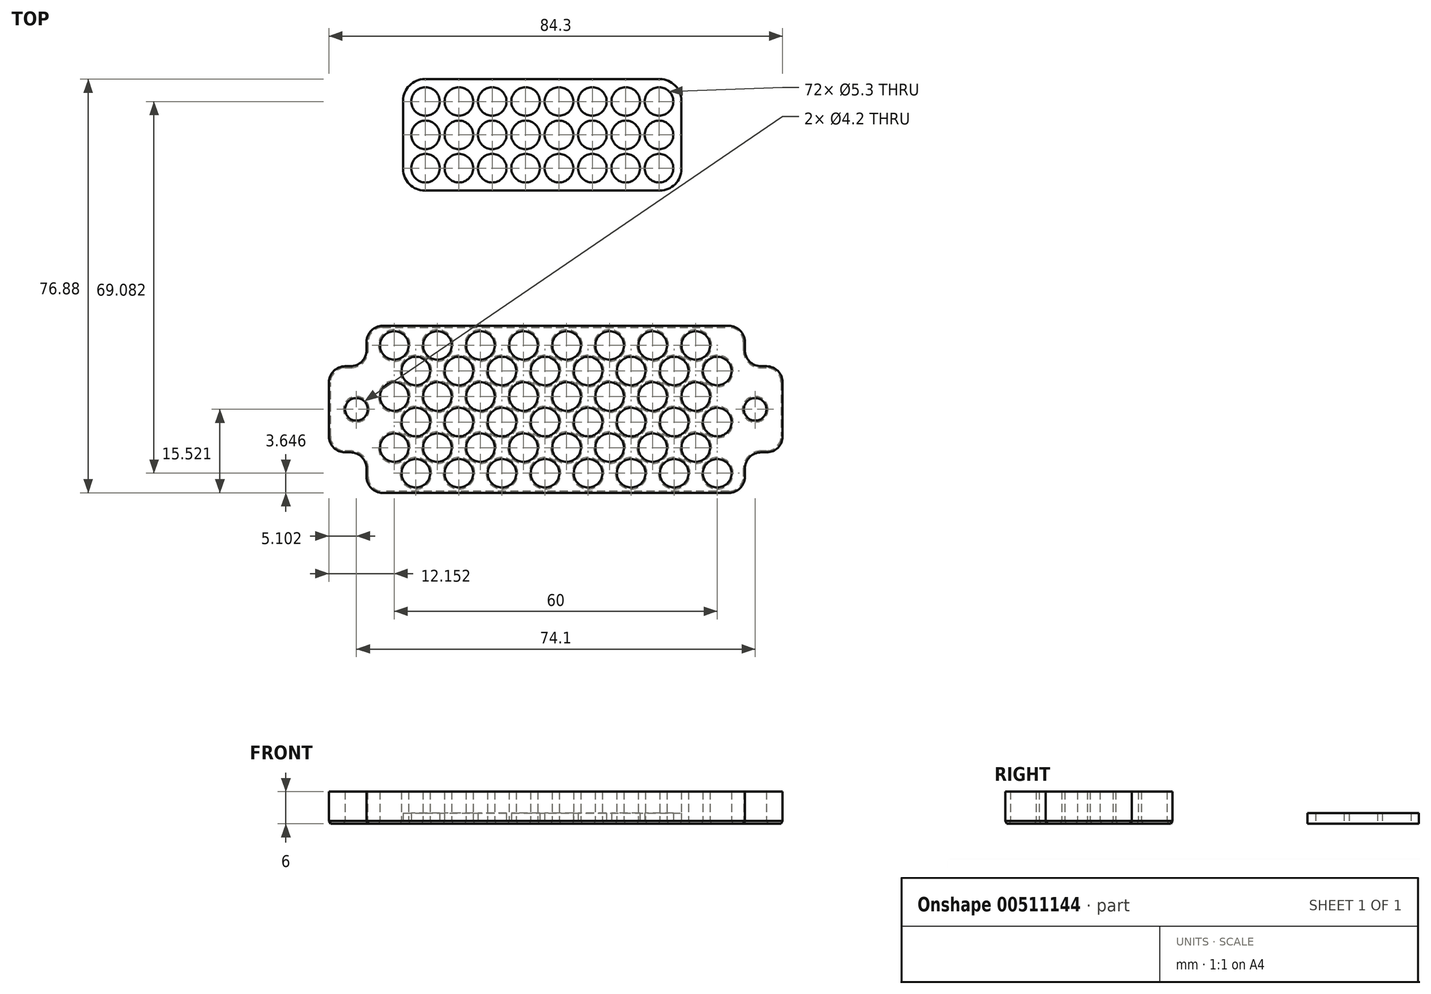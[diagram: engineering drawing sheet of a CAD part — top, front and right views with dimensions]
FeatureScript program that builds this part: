
annotation { "Feature Type Name" : "Feature", "Feature Type Description" : "" }
export const myFeature = defineFeature(function(context is Context, id is Id, definition is map)
    precondition{}
    {
        {
            var Q0;
            Q0=qCreatedBy(makeId("Top.planeOp"),FACE);
            var sketch = newSketch(context, id + "F0", { "sketchPlane" : qUnion([Q0])});
            skCircle(sketch, "E0", {"center": v(-32.47, 32.1) * mm, "radius": 2.65 * mm});
            skCircle(sketch, "E1.0.1.0", {"center": v(-32.47, 25.9) * mm, "radius": 2.65 * mm});
            skCircle(sketch, "E1.0.2.0", {"center": v(-32.47, 19.7) * mm, "radius": 2.65 * mm});
            skCircle(sketch, "E1.1.0.0", {"center": v(-26.27, 32.1) * mm, "radius": 2.65 * mm});
            skCircle(sketch, "E1.1.1.0", {"center": v(-26.27, 25.9) * mm, "radius": 2.65 * mm});
            skCircle(sketch, "E1.1.2.0", {"center": v(-26.27, 19.7) * mm, "radius": 2.65 * mm});
            skCircle(sketch, "E1.2.0.0", {"center": v(-20.07, 32.1) * mm, "radius": 2.65 * mm});
            skCircle(sketch, "E1.2.1.0", {"center": v(-20.07, 25.9) * mm, "radius": 2.65 * mm});
            skCircle(sketch, "E1.2.2.0", {"center": v(-20.07, 19.7) * mm, "radius": 2.65 * mm});
            skCircle(sketch, "E1.3.0.0", {"center": v(-13.87, 32.1) * mm, "radius": 2.65 * mm});
            skCircle(sketch, "E1.3.1.0", {"center": v(-13.87, 25.9) * mm, "radius": 2.65 * mm});
            skCircle(sketch, "E1.3.2.0", {"center": v(-13.87, 19.7) * mm, "radius": 2.65 * mm});
            skCircle(sketch, "E1.4.0.0", {"center": v(-7.67, 32.1) * mm, "radius": 2.65 * mm});
            skCircle(sketch, "E1.4.1.0", {"center": v(-7.67, 25.9) * mm, "radius": 2.65 * mm});
            skCircle(sketch, "E1.4.2.0", {"center": v(-7.67, 19.7) * mm, "radius": 2.65 * mm});
            skCircle(sketch, "E1.5.0.0", {"center": v(-1.47, 32.1) * mm, "radius": 2.65 * mm});
            skCircle(sketch, "E1.5.1.0", {"center": v(-1.47, 25.9) * mm, "radius": 2.65 * mm});
            skCircle(sketch, "E1.5.2.0", {"center": v(-1.47, 19.7) * mm, "radius": 2.65 * mm});
            skCircle(sketch, "E1.6.0.0", {"center": v(4.73, 32.1) * mm, "radius": 2.65 * mm});
            skCircle(sketch, "E1.6.1.0", {"center": v(4.73, 25.9) * mm, "radius": 2.65 * mm});
            skCircle(sketch, "E1.6.2.0", {"center": v(4.73, 19.7) * mm, "radius": 2.65 * mm});
            skCircle(sketch, "E1.7.0.0", {"center": v(10.93, 32.1) * mm, "radius": 2.65 * mm});
            skCircle(sketch, "E1.7.1.0", {"center": v(10.93, 25.9) * mm, "radius": 2.65 * mm});
            skCircle(sketch, "E1.7.2.0", {"center": v(10.93, 19.7) * mm, "radius": 2.65 * mm});
            skLineSegment(sketch, "E1.direction1", {"start": v(-32.47, 32.1) * mm, "end": v(-26.27, 32.1) * mm, "construction": true});
            skLineSegment(sketch, "E1.direction2", {"start": v(-32.47, 32.1) * mm, "end": v(-32.47, 25.9) * mm, "construction": true});
            skLineSegment(sketch, "E2.bottom", {"start": v(-32.62, 36.25) * mm, "end": v(11.08, 36.25) * mm});
            skLineSegment(sketch, "E2.top", {"start": v(-32.62, 15.55) * mm, "end": v(11.08, 15.55) * mm});
            skLineSegment(sketch, "E2.left", {"start": v(-36.62, 32.25) * mm, "end": v(-36.62, 19.55) * mm});
            skLineSegment(sketch, "E2.right", {"start": v(15.08, 32.25) * mm, "end": v(15.08, 19.55) * mm});
            skPoint(sketch, "E3.visualSharp", {"position": v(-36.62, 36.25) * mm});
            skArc(sketch, "E3.filletArc", {"start": v(-32.62, 36.25) * mm, "mid": v(-35.45, 35.08) * mm, "end": v(-36.62, 32.25) * mm});
            skPoint(sketch, "E4.visualSharp", {"position": v(-36.62, 15.55) * mm});
            skArc(sketch, "E4.filletArc", {"start": v(-36.62, 19.55) * mm, "mid": v(-35.45, 16.72) * mm, "end": v(-32.62, 15.55) * mm});
            skPoint(sketch, "E5.visualSharp", {"position": v(15.08, 15.55) * mm});
            skArc(sketch, "E5.filletArc", {"start": v(11.08, 15.55) * mm, "mid": v(13.9, 16.72) * mm, "end": v(15.08, 19.55) * mm});
            skPoint(sketch, "E6.visualSharp", {"position": v(15.08, 36.25) * mm});
            skArc(sketch, "E6.filletArc", {"start": v(15.08, 32.25) * mm, "mid": v(13.9, 35.08) * mm, "end": v(11.08, 36.25) * mm});
            skCircle(sketch, "E7", {"center": v(-38.27, -13.23) * mm, "radius": 2.65 * mm});
            skCircle(sketch, "E8", {"center": v(-34.27, -17.98) * mm, "radius": 2.65 * mm});
            skCircle(sketch, "E9.0.1.0", {"center": v(-38.27, -22.73) * mm, "radius": 2.65 * mm});
            skCircle(sketch, "E9.0.1.1", {"center": v(-34.27, -27.48) * mm, "radius": 2.65 * mm});
            skCircle(sketch, "E9.0.2.0", {"center": v(-38.27, -32.23) * mm, "radius": 2.65 * mm});
            skCircle(sketch, "E9.0.2.1", {"center": v(-34.27, -36.98) * mm, "radius": 2.65 * mm});
            skLineSegment(sketch, "E9.direction1", {"start": v(-38.27, -13.23) * mm, "end": v(-13.27, -13.23) * mm, "construction": true});
            skLineSegment(sketch, "E9.direction2", {"start": v(-38.27, -13.23) * mm, "end": v(-38.27, -22.73) * mm, "construction": true});
            skCircle(sketch, "E10.1.0.0", {"center": v(-30.27, -13.23) * mm, "radius": 2.65 * mm});
            skCircle(sketch, "E10.1.0.1", {"center": v(-26.27, -17.98) * mm, "radius": 2.65 * mm});
            skCircle(sketch, "E10.1.0.2", {"center": v(-30.27, -22.73) * mm, "radius": 2.65 * mm});
            skCircle(sketch, "E10.1.0.3", {"center": v(-26.27, -27.48) * mm, "radius": 2.65 * mm});
            skCircle(sketch, "E10.1.0.4", {"center": v(-30.27, -32.23) * mm, "radius": 2.65 * mm});
            skCircle(sketch, "E10.1.0.5", {"center": v(-26.27, -36.98) * mm, "radius": 2.65 * mm});
            skCircle(sketch, "E10.2.0.0", {"center": v(-22.27, -13.23) * mm, "radius": 2.65 * mm});
            skCircle(sketch, "E10.2.0.1", {"center": v(-18.27, -17.98) * mm, "radius": 2.65 * mm});
            skCircle(sketch, "E10.2.0.2", {"center": v(-22.27, -22.73) * mm, "radius": 2.65 * mm});
            skCircle(sketch, "E10.2.0.3", {"center": v(-18.27, -27.48) * mm, "radius": 2.65 * mm});
            skCircle(sketch, "E10.2.0.4", {"center": v(-22.27, -32.23) * mm, "radius": 2.65 * mm});
            skCircle(sketch, "E10.2.0.5", {"center": v(-18.27, -36.98) * mm, "radius": 2.65 * mm});
            skCircle(sketch, "E10.3.0.0", {"center": v(-14.27, -13.23) * mm, "radius": 2.65 * mm});
            skCircle(sketch, "E10.3.0.1", {"center": v(-10.27, -17.98) * mm, "radius": 2.65 * mm});
            skCircle(sketch, "E10.3.0.2", {"center": v(-14.27, -22.73) * mm, "radius": 2.65 * mm});
            skCircle(sketch, "E10.3.0.3", {"center": v(-10.27, -27.48) * mm, "radius": 2.65 * mm});
            skCircle(sketch, "E10.3.0.4", {"center": v(-14.27, -32.23) * mm, "radius": 2.65 * mm});
            skCircle(sketch, "E10.3.0.5", {"center": v(-10.27, -36.98) * mm, "radius": 2.65 * mm});
            skCircle(sketch, "E10.4.0.0", {"center": v(-6.27, -13.23) * mm, "radius": 2.65 * mm});
            skCircle(sketch, "E10.4.0.1", {"center": v(-2.27, -17.98) * mm, "radius": 2.65 * mm});
            skCircle(sketch, "E10.4.0.2", {"center": v(-6.27, -22.73) * mm, "radius": 2.65 * mm});
            skCircle(sketch, "E10.4.0.3", {"center": v(-2.27, -27.48) * mm, "radius": 2.65 * mm});
            skCircle(sketch, "E10.4.0.4", {"center": v(-6.27, -32.23) * mm, "radius": 2.65 * mm});
            skCircle(sketch, "E10.4.0.5", {"center": v(-2.27, -36.98) * mm, "radius": 2.65 * mm});
            skCircle(sketch, "E10.5.0.0", {"center": v(1.73, -13.23) * mm, "radius": 2.65 * mm});
            skCircle(sketch, "E10.5.0.1", {"center": v(5.73, -17.98) * mm, "radius": 2.65 * mm});
            skCircle(sketch, "E10.5.0.2", {"center": v(1.73, -22.73) * mm, "radius": 2.65 * mm});
            skCircle(sketch, "E10.5.0.3", {"center": v(5.73, -27.48) * mm, "radius": 2.65 * mm});
            skCircle(sketch, "E10.5.0.4", {"center": v(1.73, -32.23) * mm, "radius": 2.65 * mm});
            skCircle(sketch, "E10.5.0.5", {"center": v(5.73, -36.98) * mm, "radius": 2.65 * mm});
            skCircle(sketch, "E10.6.0.0", {"center": v(9.73, -13.23) * mm, "radius": 2.65 * mm});
            skCircle(sketch, "E10.6.0.1", {"center": v(13.73, -17.98) * mm, "radius": 2.65 * mm});
            skCircle(sketch, "E10.6.0.2", {"center": v(9.73, -22.73) * mm, "radius": 2.65 * mm});
            skCircle(sketch, "E10.6.0.3", {"center": v(13.73, -27.48) * mm, "radius": 2.65 * mm});
            skCircle(sketch, "E10.6.0.4", {"center": v(9.73, -32.23) * mm, "radius": 2.65 * mm});
            skCircle(sketch, "E10.6.0.5", {"center": v(13.73, -36.98) * mm, "radius": 2.65 * mm});
            skCircle(sketch, "E10.7.0.0", {"center": v(17.73, -13.23) * mm, "radius": 2.65 * mm});
            skCircle(sketch, "E10.7.0.1", {"center": v(21.73, -17.98) * mm, "radius": 2.65 * mm});
            skCircle(sketch, "E10.7.0.2", {"center": v(17.73, -22.73) * mm, "radius": 2.65 * mm});
            skCircle(sketch, "E10.7.0.3", {"center": v(21.73, -27.48) * mm, "radius": 2.65 * mm});
            skCircle(sketch, "E10.7.0.4", {"center": v(17.73, -32.23) * mm, "radius": 2.65 * mm});
            skCircle(sketch, "E10.7.0.5", {"center": v(21.73, -36.98) * mm, "radius": 2.65 * mm});
            skLineSegment(sketch, "E10.direction1", {"start": v(-38.27, -13.23) * mm, "end": v(-30.27, -13.23) * mm, "construction": true});
            skLineSegment(sketch, "E11", {"start": v(-30.27, -10.58) * mm, "end": v(-47.9, -10.58) * mm, "construction": true});
            skLineSegment(sketch, "E12", {"start": v(-34.27, -39.63) * mm, "end": v(-49.47, -39.63) * mm, "construction": true});
            skLineSegment(sketch, "E13", {"start": v(-40.92, -13.23) * mm, "end": v(-40.92, -3.23) * mm, "construction": true});
            skLineSegment(sketch, "E14", {"start": v(24.38, -17.98) * mm, "end": v(24.38, -1.9) * mm, "construction": true});
            skLineSegment(sketch, "E15.bottom", {"start": v(-43.42, -9.58) * mm, "end": v(26.88, -9.58) * mm});
            skLineSegment(sketch, "E15.top", {"start": v(-43.42, -40.63) * mm, "end": v(26.88, -40.63) * mm});
            skLineSegment(sketch, "E15.left", {"start": v(-43.42, -9.58) * mm, "end": v(-43.42, -40.63) * mm});
            skLineSegment(sketch, "E15.right", {"start": v(26.88, -9.58) * mm, "end": v(26.88, -40.63) * mm});
            skLineSegment(sketch, "E16.bottom", {"start": v(-43.42, -33.1) * mm, "end": v(-50.42, -33.1) * mm});
            skLineSegment(sketch, "E16.top", {"start": v(-43.42, -17.1) * mm, "end": v(-50.42, -17.1) * mm});
            skLineSegment(sketch, "E16.left", {"start": v(-43.42, -33.1) * mm, "end": v(-43.42, -17.1) * mm});
            skLineSegment(sketch, "E16.right", {"start": v(-50.42, -33.1) * mm, "end": v(-50.42, -17.1) * mm});
            skPoint(sketch, "E16.middle", {"position": v(-46.92, -25.1) * mm});
            skPoint(sketch, "E16.middle.positionSnap0", {"position": v(-43.42, -25.1) * mm});
            skPoint(sketch, "E16.centerSnap0", {"position": v(-43.42, -25.1) * mm});
            skLineSegment(sketch, "E17.bottom", {"start": v(26.88, -17.1) * mm, "end": v(33.88, -17.1) * mm});
            skLineSegment(sketch, "E17.top", {"start": v(26.88, -33.1) * mm, "end": v(33.88, -33.1) * mm});
            skLineSegment(sketch, "E17.left", {"start": v(26.88, -17.1) * mm, "end": v(26.88, -33.1) * mm});
            skLineSegment(sketch, "E17.right", {"start": v(33.88, -17.1) * mm, "end": v(33.88, -33.1) * mm});
            skPoint(sketch, "E17.middle", {"position": v(30.38, -25.1) * mm});
            skCircle(sketch, "E18", {"center": v(-45.32, -25.1) * mm, "radius": 2.1 * mm});
            skCircle(sketch, "E19", {"center": v(28.78, -25.1) * mm, "radius": 2.1 * mm});
            skSolve(sketch);
        }
        {
            var Q0;
            Q0=makeQuery(id+"F0.imprint","IMPRINT",FACE,{"disambiguationData":[TD([[makeQuery(id+"F0.imprint","IMPRINT",EDGE,{"derivedFrom":sQuery(id+"F0.wireOp",EDGE,"E0")}),-1.0]])]});
            extrude(context, id + "F1", {"entities" : qUnion([Q0]), "depth" : 2 * mm});
        }
        {
            var Q0;
            Q0=makeQuery(id+"F0.imprint","IMPRINT",FACE,{"disambiguationData":[TD([[makeQuery(id+"F0.imprint","IMPRINT",EDGE,{"derivedFrom":sQuery(id+"F0.wireOp",EDGE,"E7")}),-1.0]])]});
            var Q1;
            Q1=makeQuery(id+"F0.imprint","IMPRINT",FACE,{"disambiguationData":[TD([[makeQuery(id+"F0.imprint","IMPRINT",EDGE,{"derivedFrom":sQuery(id+"F0.wireOp",EDGE,"E16.bottom")}),-1.0]])]});
            var Q2;
            Q2=makeQuery(id+"F0.imprint","IMPRINT",FACE,{"disambiguationData":[TD([[makeQuery(id+"F0.imprint","IMPRINT",EDGE,{"derivedFrom":sQuery(id+"F0.wireOp",EDGE,"E17.bottom")}),-1.0]])]});
            extrude(context, id + "F2", {"entities" : qUnion([Q0, Q1, Q2]), "depth" : 6 * mm});
        }
        {
            var Q0;
            Q0=makeQuery(id+"F2.opExtrude","SWEPT_EDGE",EDGE,{"disambiguationData":[OSD([sQuery(id+"F0.wireOp",EDGE,"E15.bottom"),sQuery(id+"F0.wireOp",EDGE,"E15.left")])]});
            var Q1;
            Q1=makeQuery(id+"F2.opExtrude","SWEPT_EDGE",EDGE,{"disambiguationData":[OSD([sQuery(id+"F0.wireOp",EDGE,"E15.top"),sQuery(id+"F0.wireOp",EDGE,"E15.left")])]});
            var Q2;
            Q2=makeQuery(id+"F2.opExtrude","SWEPT_EDGE",EDGE,{"disambiguationData":[OSD([sQuery(id+"F0.wireOp",EDGE,"E15.top"),sQuery(id+"F0.wireOp",EDGE,"E15.right")])]});
            var Q3;
            Q3=makeQuery(id+"F2.opExtrude","SWEPT_EDGE",EDGE,{"disambiguationData":[OSD([sQuery(id+"F0.wireOp",EDGE,"E15.bottom"),sQuery(id+"F0.wireOp",EDGE,"E15.right")])]});
            var Q4;
            Q4=makeQuery(id+"F2.opExtrude","SWEPT_EDGE",EDGE,{"disambiguationData":[OSD([sQuery(id+"F0.wireOp",EDGE,"E15.left"),sQuery(id+"F0.wireOp",EDGE,"E16.top"),sQuery(id+"F0.wireOp",EDGE,"E16.left")])]});
            var Q5;
            Q5=makeQuery(id+"F2.opExtrude","SWEPT_EDGE",EDGE,{"disambiguationData":[OSD([sQuery(id+"F0.wireOp",EDGE,"E16.top"),sQuery(id+"F0.wireOp",EDGE,"E16.right")])]});
            var Q6;
            Q6=makeQuery(id+"F2.opExtrude","SWEPT_EDGE",EDGE,{"disambiguationData":[OSD([sQuery(id+"F0.wireOp",EDGE,"E16.bottom"),sQuery(id+"F0.wireOp",EDGE,"E16.right")])]});
            var Q7;
            Q7=makeQuery(id+"F2.opExtrude","SWEPT_EDGE",EDGE,{"disambiguationData":[OSD([sQuery(id+"F0.wireOp",EDGE,"E15.left"),sQuery(id+"F0.wireOp",EDGE,"E16.bottom"),sQuery(id+"F0.wireOp",EDGE,"E16.left")])]});
            var Q8;
            Q8=makeQuery(id+"F2.opExtrude","SWEPT_EDGE",EDGE,{"disambiguationData":[OSD([sQuery(id+"F0.wireOp",EDGE,"E15.right"),sQuery(id+"F0.wireOp",EDGE,"E17.top"),sQuery(id+"F0.wireOp",EDGE,"E17.left")])]});
            var Q9;
            Q9=makeQuery(id+"F2.opExtrude","SWEPT_EDGE",EDGE,{"disambiguationData":[OSD([sQuery(id+"F0.wireOp",EDGE,"E17.top"),sQuery(id+"F0.wireOp",EDGE,"E17.right")])]});
            var Q10;
            Q10=makeQuery(id+"F2.opExtrude","SWEPT_EDGE",EDGE,{"disambiguationData":[OSD([sQuery(id+"F0.wireOp",EDGE,"E17.bottom"),sQuery(id+"F0.wireOp",EDGE,"E17.right")])]});
            var Q11;
            Q11=makeQuery(id+"F2.opExtrude","SWEPT_EDGE",EDGE,{"disambiguationData":[OSD([sQuery(id+"F0.wireOp",EDGE,"E15.right"),sQuery(id+"F0.wireOp",EDGE,"E17.bottom"),sQuery(id+"F0.wireOp",EDGE,"E17.left")])]});
            fillet(context, id + "F3", {"entities" : qUnion([Q0, Q1, Q2, Q3, Q4, Q5, Q6, Q7, Q8, Q9, Q10, Q11]), "radius" : 3 * mm, "tangentPropagation" : true, "allowEdgeOverflow" : false});
        }
        {
            var Q0;
            Q0=makeQuery(id+"F2.opExtrude","CAP_FACE",FACE,{"disambiguationData":[OSD([sQuery(id+"F0.wireOp",EDGE,"E7"),sQuery(id+"F0.wireOp",EDGE,"E8"),sQuery(id+"F0.wireOp",EDGE,"E9.0.1.0"),sQuery(id+"F0.wireOp",EDGE,"E9.0.1.1"),sQuery(id+"F0.wireOp",EDGE,"E9.0.2.0"),sQuery(id+"F0.wireOp",EDGE,"E9.0.2.1"),sQuery(id+"F0.wireOp",EDGE,"E10.1.0.0"),sQuery(id+"F0.wireOp",EDGE,"E10.1.0.1"),sQuery(id+"F0.wireOp",EDGE,"E10.1.0.2"),sQuery(id+"F0.wireOp",EDGE,"E10.1.0.3"),sQuery(id+"F0.wireOp",EDGE,"E10.1.0.4"),sQuery(id+"F0.wireOp",EDGE,"E10.1.0.5"),sQuery(id+"F0.wireOp",EDGE,"E10.2.0.0"),sQuery(id+"F0.wireOp",EDGE,"E10.2.0.1"),sQuery(id+"F0.wireOp",EDGE,"E10.2.0.2"),sQuery(id+"F0.wireOp",EDGE,"E10.2.0.3"),sQuery(id+"F0.wireOp",EDGE,"E10.2.0.4"),sQuery(id+"F0.wireOp",EDGE,"E10.2.0.5"),sQuery(id+"F0.wireOp",EDGE,"E10.3.0.0"),sQuery(id+"F0.wireOp",EDGE,"E10.3.0.1"),sQuery(id+"F0.wireOp",EDGE,"E10.3.0.2"),sQuery(id+"F0.wireOp",EDGE,"E10.3.0.3"),sQuery(id+"F0.wireOp",EDGE,"E10.3.0.4"),sQuery(id+"F0.wireOp",EDGE,"E10.3.0.5"),sQuery(id+"F0.wireOp",EDGE,"E10.4.0.0"),sQuery(id+"F0.wireOp",EDGE,"E10.4.0.1"),sQuery(id+"F0.wireOp",EDGE,"E10.4.0.2"),sQuery(id+"F0.wireOp",EDGE,"E10.4.0.3"),sQuery(id+"F0.wireOp",EDGE,"E10.4.0.4"),sQuery(id+"F0.wireOp",EDGE,"E10.4.0.5"),sQuery(id+"F0.wireOp",EDGE,"E10.5.0.0"),sQuery(id+"F0.wireOp",EDGE,"E10.5.0.1"),sQuery(id+"F0.wireOp",EDGE,"E10.5.0.2"),sQuery(id+"F0.wireOp",EDGE,"E10.5.0.3"),sQuery(id+"F0.wireOp",EDGE,"E10.5.0.4"),sQuery(id+"F0.wireOp",EDGE,"E10.5.0.5"),sQuery(id+"F0.wireOp",EDGE,"E10.6.0.0"),sQuery(id+"F0.wireOp",EDGE,"E10.6.0.1"),sQuery(id+"F0.wireOp",EDGE,"E10.6.0.2"),sQuery(id+"F0.wireOp",EDGE,"E10.6.0.3"),sQuery(id+"F0.wireOp",EDGE,"E10.6.0.4"),sQuery(id+"F0.wireOp",EDGE,"E10.6.0.5"),sQuery(id+"F0.wireOp",EDGE,"E10.7.0.0"),sQuery(id+"F0.wireOp",EDGE,"E10.7.0.1"),sQuery(id+"F0.wireOp",EDGE,"E10.7.0.2"),sQuery(id+"F0.wireOp",EDGE,"E10.7.0.3"),sQuery(id+"F0.wireOp",EDGE,"E10.7.0.4"),sQuery(id+"F0.wireOp",EDGE,"E10.7.0.5"),sQuery(id+"F0.wireOp",EDGE,"E15.bottom"),sQuery(id+"F0.wireOp",EDGE,"E15.top"),sQuery(id+"F0.wireOp",EDGE,"E15.left"),sQuery(id+"F0.wireOp",EDGE,"E15.right"),sQuery(id+"F0.wireOp",EDGE,"E16.bottom"),sQuery(id+"F0.wireOp",EDGE,"E16.top"),sQuery(id+"F0.wireOp",EDGE,"E16.right"),sQuery(id+"F0.wireOp",EDGE,"E17.bottom"),sQuery(id+"F0.wireOp",EDGE,"E17.top"),sQuery(id+"F0.wireOp",EDGE,"E17.right"),sQuery(id+"F0.wireOp",EDGE,"E18"),sQuery(id+"F0.wireOp",EDGE,"E19")])],"isStart":true});
            chamfer(context, id + "F4", {"entities" : qUnion([Q0]), "chamferType" : ChamferType.OFFSET_ANGLE, "width" : 0.3 * mm, "oppositeDirection" : false, "angle" : 60 * degree, "tangentPropagation" : true});
        }
    });
